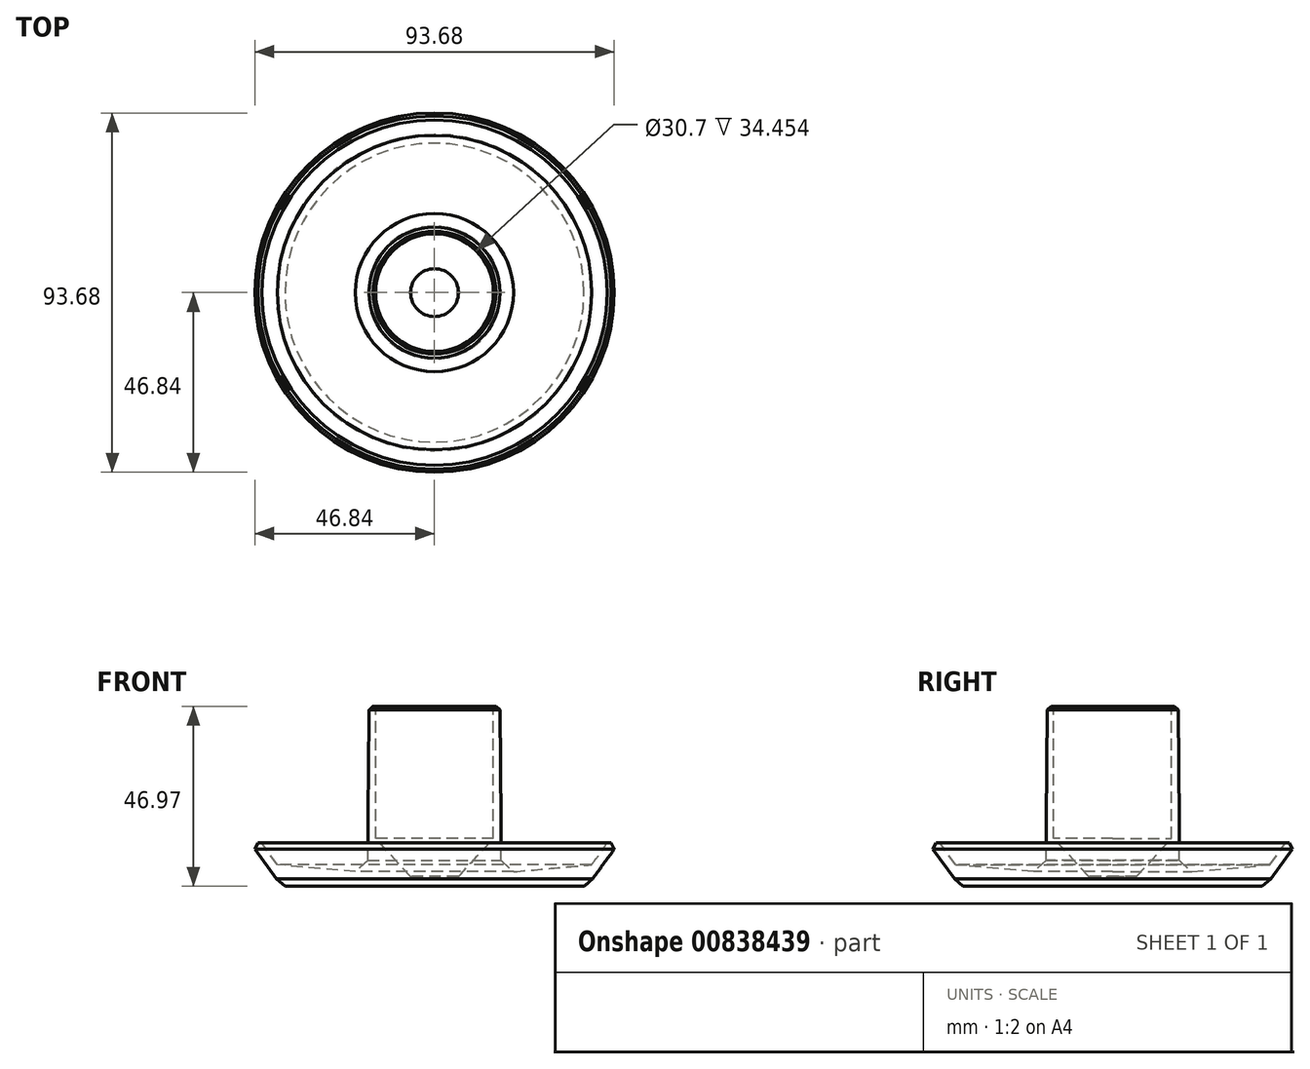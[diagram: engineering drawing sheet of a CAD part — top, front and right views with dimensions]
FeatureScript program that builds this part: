
annotation { "Feature Type Name" : "Feature", "Feature Type Description" : "" }
export const myFeature = defineFeature(function(context is Context, id is Id, definition is map)
    precondition{}
    {
        {
            var Q0;
            Q0=qCreatedBy(makeId("Front.planeOp"),FACE);
            var sketch = newSketch(context, id + "F0", { "sketchPlane" : qUnion([Q0])});
            skLineSegment(sketch, "E0", {"start": v(0, 0) * mm, "end": v(35, 0) * mm});
            skLineSegment(sketch, "E1", {"start": v(45, 9.3) * mm, "end": v(48, 9.3) * mm});
            skLineSegment(sketch, "E2", {"start": v(48, 9.3) * mm, "end": v(41.24, 0) * mm});
            skLineSegment(sketch, "E3", {"start": v(41.24, 0) * mm, "end": v(35, 0) * mm});
            skLineSegment(sketch, "E4", {"start": v(45, 9.3) * mm, "end": v(40.97, 3.63) * mm});
            skLineSegment(sketch, "E5", {"start": v(40.97, 3.63) * mm, "end": v(0, 0) * mm});
            skLineSegment(sketch, "E6", {"start": v(0, 0) * mm, "end": v(17.35, 0) * mm});
            skLineSegment(sketch, "E7", {"start": v(17.35, 0) * mm, "end": v(17.35, 44.97) * mm});
            skLineSegment(sketch, "E8", {"start": v(17.35, 44.97) * mm, "end": v(15.35, 44.97) * mm});
            skLineSegment(sketch, "E9", {"start": v(15.35, 44.97) * mm, "end": v(15.35, 0) * mm});
            skLineSegment(sketch, "E10", {"start": v(41.24, 0) * mm, "end": v(38.98, -2) * mm});
            skLineSegment(sketch, "E11", {"start": v(38.98, -2) * mm, "end": v(0, -2) * mm});
            skLineSegment(sketch, "E12", {"start": v(0, -2) * mm, "end": v(0, 0) * mm});
            skLineSegment(sketch, "E13", {"start": v(0, 51.21) * mm, "end": v(0, -19.36) * mm});
            skSolve(sketch);
        }
        {
            var Q0;
            Q0 = qSketchRegion(id + "F0", true);
            var Q1;
            Q1=sQuery(id+"F0.wireOp",EDGE,"E13");
            revolve(context, id + "F1", {"surfaceOperationType" : NewSurfaceOperationType.NEW, "entities" : qUnion([Q0]), "axis" : qUnion([Q1]), "revolveType" : RevolveType.FULL});
        }
        {
            var Q0;
            Q0=makeQuery(id+"F1.opRevolve","SWEPT_EDGE",EDGE,{"disambiguationData":[OSD([sQuery(id+"F0.wireOp",EDGE,"E5"),sQuery(id+"F0.wireOp",EDGE,"E9")])]});
            chamfer(context, id + "F2", {"entities" : qUnion([Q0]), "width" : 10 * mm, "tangentPropagation" : true});
        }
        {
            var Q0;
            Q0=makeQuery(id+"F1.opRevolve","SWEPT_EDGE",EDGE,{"disambiguationData":[OSD([sQuery(id+"F0.wireOp",EDGE,"E5"),sQuery(id+"F0.wireOp",EDGE,"E7")])]});
            chamfer(context, id + "F3", {"entities" : qUnion([Q0]), "width" : 3 * mm, "tangentPropagation" : true});
        }
        {
            var Q0;
            Q0=makeQuery(id+"F1.opRevolve","SWEPT_EDGE",EDGE,{"disambiguationData":[OSD([sQuery(id+"F0.wireOp",EDGE,"E7"),sQuery(id+"F0.wireOp",EDGE,"E8")])]});
            chamfer(context, id + "F4", {"entities" : qUnion([Q0]), "chamferType" : ChamferType.TWO_OFFSETS, "width1" : 0.3 * mm, "oppositeDirection" : false, "width2" : 30 * mm, "tangentPropagation" : true});
        }
        {
            var Q0;
            Q0=makeQuery(id+"F1.opRevolve","SWEPT_EDGE",EDGE,{"disambiguationData":[OSD([sQuery(id+"F0.wireOp",EDGE,"E1"),sQuery(id+"F0.wireOp",EDGE,"E2")])]});
            chamfer(context, id + "F5", {"entities" : qUnion([Q0]), "width" : 1 * mm, "tangentPropagation" : true});
        }
        {
            var Q0;
            {var subQ0=sQuery(id+"F0.wireOp",EDGE,"E8");Q0=makeQuery(id+"F4.opChamfer","BLEND_EDGE",EDGE,{"blendedFrom":[makeQuery(id+"F1.opRevolve","SWEPT_EDGE",EDGE,{"disambiguationData":[OSD([sQuery(id+"F0.wireOp",EDGE,"E7"),subQ0])]}),makeQuery(id+"F1.opRevolve","SWEPT_FACE",FACE,{"disambiguationData":[OSD([subQ0])]})],"blendedInto":[makeQuery(id+"F1.opRevolve","SWEPT_FACE",FACE,{"disambiguationData":[OSD([subQ0])]})]});}
            chamfer(context, id + "F6", {"entities" : qUnion([Q0]), "width" : 1 * mm, "tangentPropagation" : true});
        }
    });
